# Revit family: Toilet-Floor_Mount-KOHLER-Brazn-K-EX22384T_1
name_source: partatom
category: Plumbing Fixtures
units: mm (PartAtom-declared; Revit-internal decimal feet)

## family parameters
Cut with Voids When Loaded = No
Host = Face
Maintain Annotation Orientation = No
OmniClass Number = 23.31.19.00
OmniClass Title = Toilets
Part Type = Normal
Room Calculation Point = No
Round Connector Dimension = Use Diameter
Shared = No

## types (2) — shared parameters
ADA Compliant = No
Assembly Code = D2010100
Bowl Height = 15 3/8"
CW Connection = Yes
Cold Water Inlet = Cold Water Inlet
Date Modified = 06/22/2022
Default Elevation = 0"
Finish = Kohler-Vitreous_China-0-White
Flow Rate = 0 GPM
Flush Rate- GPF = 0 GPF
Flush Rate- LPF = 0 GPF
HW Connection = No
Height = 29 1/2"
Hot Water Inlet = Hot Water Inlet
Manufacturer = Kohler Co.
Master Format 2014 = 22 42 13.13
Master Format 2014 Name = Residential Water Closets
Material = Vitreous China
Pressure = 0.00 psi
Product Name = Brazn
Rough-In = 15 3/4"
URL = http://www.kohler.com.cn
Vent Connection = No
Waste Connection = Yes
Waste Water Outlet = Waste Water Outlet
WaterSense Certified = No
Width = 15 3/16"

## per-type parameters (varying)
| type | Description | HC | Length | Model | SL | Seat Height | Seat Included | Type |
| With Seat, 0-White | 2PC TOILET 400MM (EXQ) | No | 28 3/4" | K-EX22384T-SL-0 | Yes | 2 1/16" | Yes | 1 |
| Without Seat, 0-White | 2PC TOILET HC 400MM W/O ST | Yes | 29 3/8" | K-EX22384T-HC-0 | No | 3 9/16" | No | 2 |

## geometry (parser evidence)
native form markers: Sweep x5
no freeform markers — native parametric forms only
